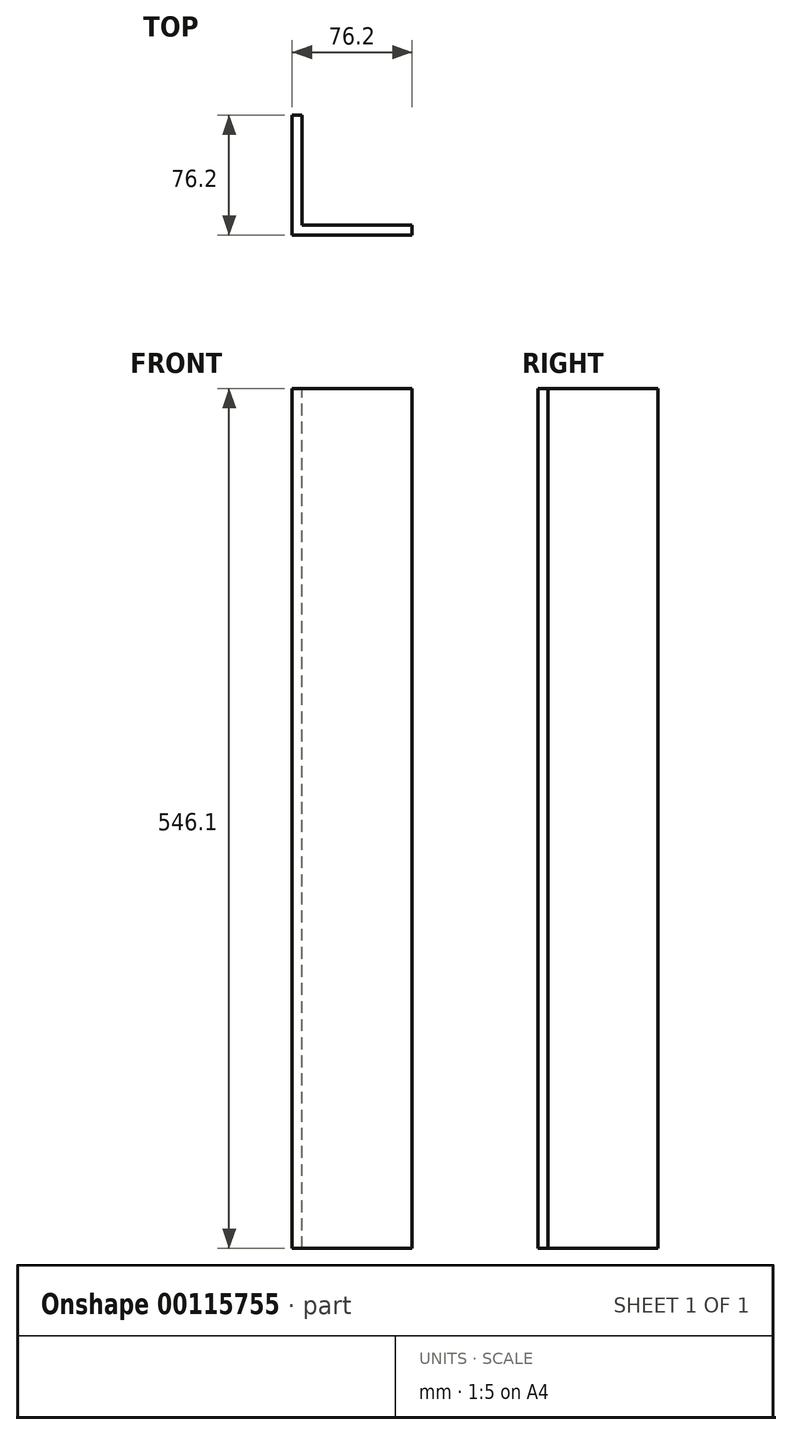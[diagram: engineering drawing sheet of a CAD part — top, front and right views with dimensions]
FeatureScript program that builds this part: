
annotation { "Feature Type Name" : "Feature", "Feature Type Description" : "" }
export const myFeature = defineFeature(function(context is Context, id is Id, definition is map)
    precondition{}
    {
        {
            var Q0;
            Q0=qCreatedBy(makeId("Top.planeOp"),FACE);
            var sketch = newSketch(context, id + "F0", { "sketchPlane" : qUnion([Q0])});
            skLineSegment(sketch, "E0", {"start": v(0, 76.2) * mm, "end": v(0, 0) * mm});
            skLineSegment(sketch, "E1", {"start": v(0, 0) * mm, "end": v(76.2, 0) * mm});
            skLineSegment(sketch, "E2.0", {"start": v(6.35, 6.35) * mm, "end": v(76.2, 6.35) * mm});
            skLineSegment(sketch, "E2.1", {"start": v(6.35, 76.2) * mm, "end": v(6.35, 6.35) * mm});
            skLineSegment(sketch, "E3", {"start": v(0, 76.2) * mm, "end": v(6.35, 76.2) * mm});
            skLineSegment(sketch, "E4", {"start": v(76.2, 6.35) * mm, "end": v(76.2, 0) * mm});
            skSolve(sketch);
        }
        {
            var Q0;
            Q0 = qSketchRegion(id + "F0", true);
            extrude(context, id + "F1", {"entities" : qUnion([Q0]), "oppositeDirection" : true, "depth" : 546.1 * mm});
        }
    });
